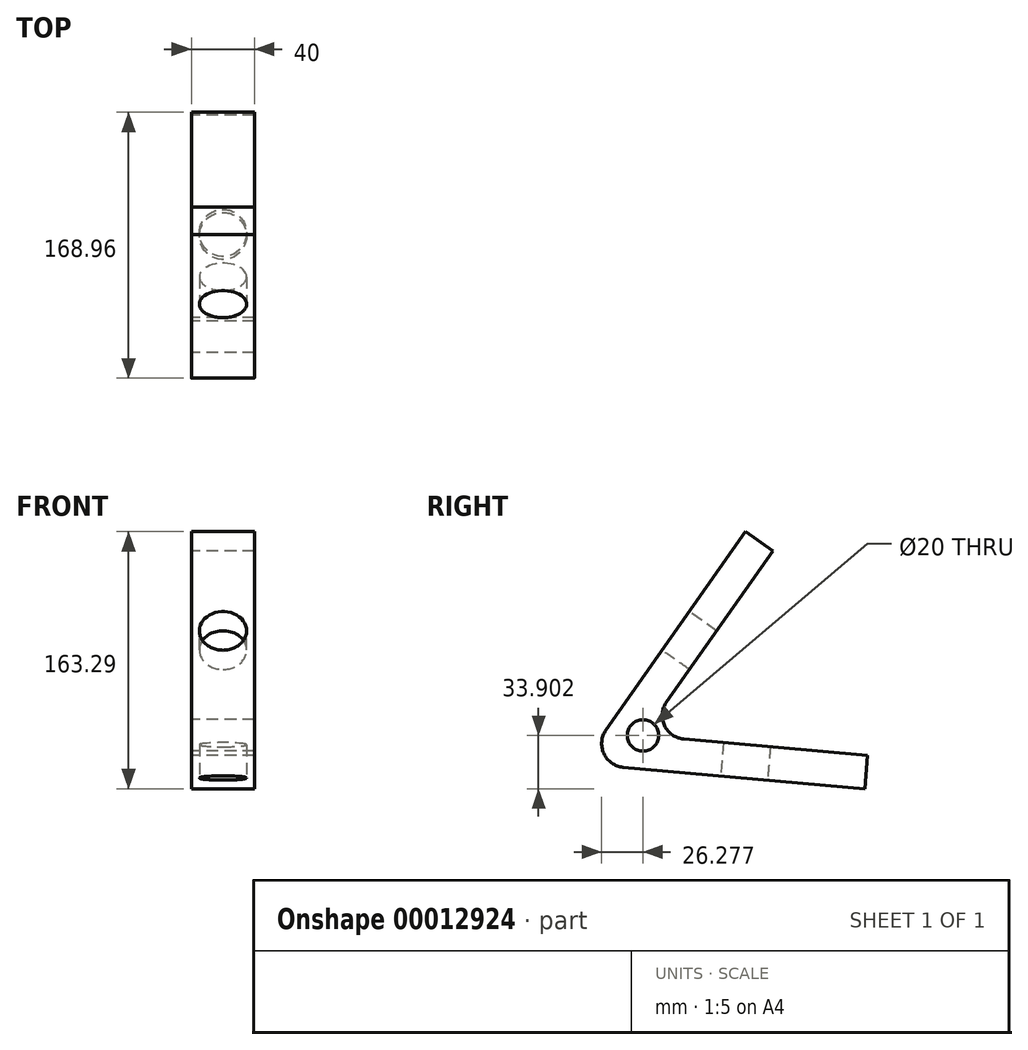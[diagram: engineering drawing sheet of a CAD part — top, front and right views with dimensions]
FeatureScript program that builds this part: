
annotation { "Feature Type Name" : "Feature", "Feature Type Description" : "" }
export const myFeature = defineFeature(function(context is Context, id is Id, definition is map)
    precondition{}
    {
        {
            var Q0;
            Q0=qCreatedBy(makeId("Right.planeOp"),FACE);
            var sketch = newSketch(context, id + "F0", { "sketchPlane" : qUnion([Q0])});
            skLineSegment(sketch, "E0", {"start": v(14.95, 21.25) * mm, "end": v(103.54, 147.24) * mm});
            skLineSegment(sketch, "E1", {"start": v(179.28, -16.05) * mm, "end": v(25.88, -2.32) * mm});
            skPoint(sketch, "E2.visualSharp", {"position": v(0, 0) * mm});
            skArc(sketch, "E2.filletArc", {"start": v(14.95, 21.25) * mm, "mid": v(13.6, 6.31) * mm, "end": v(25.88, -2.32) * mm});
            skLineSegment(sketch, "E3.0", {"start": v(53.43, 39.1) * mm, "end": v(120.9, 135.03) * mm});
            skLineSegment(sketch, "E4.0", {"start": v(181.17, 5.08) * mm, "end": v(64.36, 15.53) * mm});
            skPoint(sketch, "E5.visualSharp", {"position": v(38.49, 17.85) * mm});
            skArc(sketch, "E5.filletArc", {"start": v(53.43, 39.1) * mm, "mid": v(52.1, 24.16) * mm, "end": v(64.36, 15.53) * mm});
            skCircle(sketch, "E6", {"center": v(38.49, 17.85) * mm, "radius": 10 * mm});
            skLineSegment(sketch, "E7", {"start": v(103.54, 147.24) * mm, "end": v(120.9, 135.03) * mm});
            skLineSegment(sketch, "E8", {"start": v(181.17, 5.08) * mm, "end": v(179.28, -16.05) * mm});
            skSolve(sketch);
        }
        {
            var Q0;
            Q0=makeQuery(id+"F0.imprint","IMPRINT",FACE,{"disambiguationData":[TD([[makeQuery(id+"F0.imprint","IMPRINT",EDGE,{"derivedFrom":sQuery(id+"F0.wireOp",EDGE,"E0")}),-1.0]])]});
            extrude(context, id + "F1", {"entities" : qUnion([Q0]), "depth" : 40 * mm});
        }
        {
            var Q0;
            Q0=makeQuery(id+"F1.opExtrude","SWEPT_FACE",FACE,{"disambiguationData":[OSD([sQuery(id+"F0.wireOp",EDGE,"E1")])]});
            var sketch = newSketch(context, id + "F2", { "sketchPlane" : qUnion([Q0])});
            skCircle(sketch, "E9", {"center": v(20, -103) * mm, "radius": 15 * mm});
            skLineSegment(sketch, "E10", {"start": v(20, -180) * mm, "end": v(20, -25.98) * mm, "construction": true});
            skLineSegment(sketch, "E11", {"start": v(0, -103) * mm, "end": v(40, -103) * mm, "construction": true});
            skSolve(sketch);
        }
        {
            var Q0;
            Q0=makeQuery(id+"F2.imprint","IMPRINT",FACE,{"disambiguationData":[TD([[makeQuery(id+"F2.imprint","IMPRINT",EDGE,{"derivedFrom":sQuery(id+"F2.wireOp",EDGE,"E9")}),1.0]])]});
            var Q1;
            Q1=sQuery(id+"F2.wireOp",EDGE,"E9");
            extrude(context, id + "F3", {"entities" : qUnion([Q0]), "operationType" : NewBodyOperationType.REMOVE, "surfaceEntities" : qUnion([Q1]), "endBound" : BoundingType.UP_TO_NEXT, "oppositeDirection" : true, "depth" : 25 * mm});
        }
        {
            var Q0;
            Q0=makeQuery(id+"F1.opExtrude","SWEPT_FACE",FACE,{"disambiguationData":[OSD([sQuery(id+"F0.wireOp",EDGE,"E0")])]});
            var sketch = newSketch(context, id + "F4", { "sketchPlane" : qUnion([Q0])});
            skLineSegment(sketch, "E12", {"start": v(20, 25.98) * mm, "end": v(20, 180) * mm, "construction": true});
            skLineSegment(sketch, "E13", {"start": v(0, 103) * mm, "end": v(40, 103) * mm, "construction": true});
            skCircle(sketch, "E14", {"center": v(20, 103) * mm, "radius": 15 * mm});
            skSolve(sketch);
        }
        {
            var Q0;
            Q0=makeQuery(id+"F4.imprint","IMPRINT",FACE,{"disambiguationData":[TD([[makeQuery(id+"F4.imprint","IMPRINT",EDGE,{"derivedFrom":sQuery(id+"F4.wireOp",EDGE,"E14")}),1.0]])]});
            var Q1;
            Q1=sQuery(id+"F4.wireOp",EDGE,"E14");
            extrude(context, id + "F5", {"entities" : qUnion([Q0]), "operationType" : NewBodyOperationType.REMOVE, "surfaceEntities" : qUnion([Q1]), "endBound" : BoundingType.UP_TO_NEXT, "oppositeDirection" : true, "depth" : 25 * mm});
        }
    });
